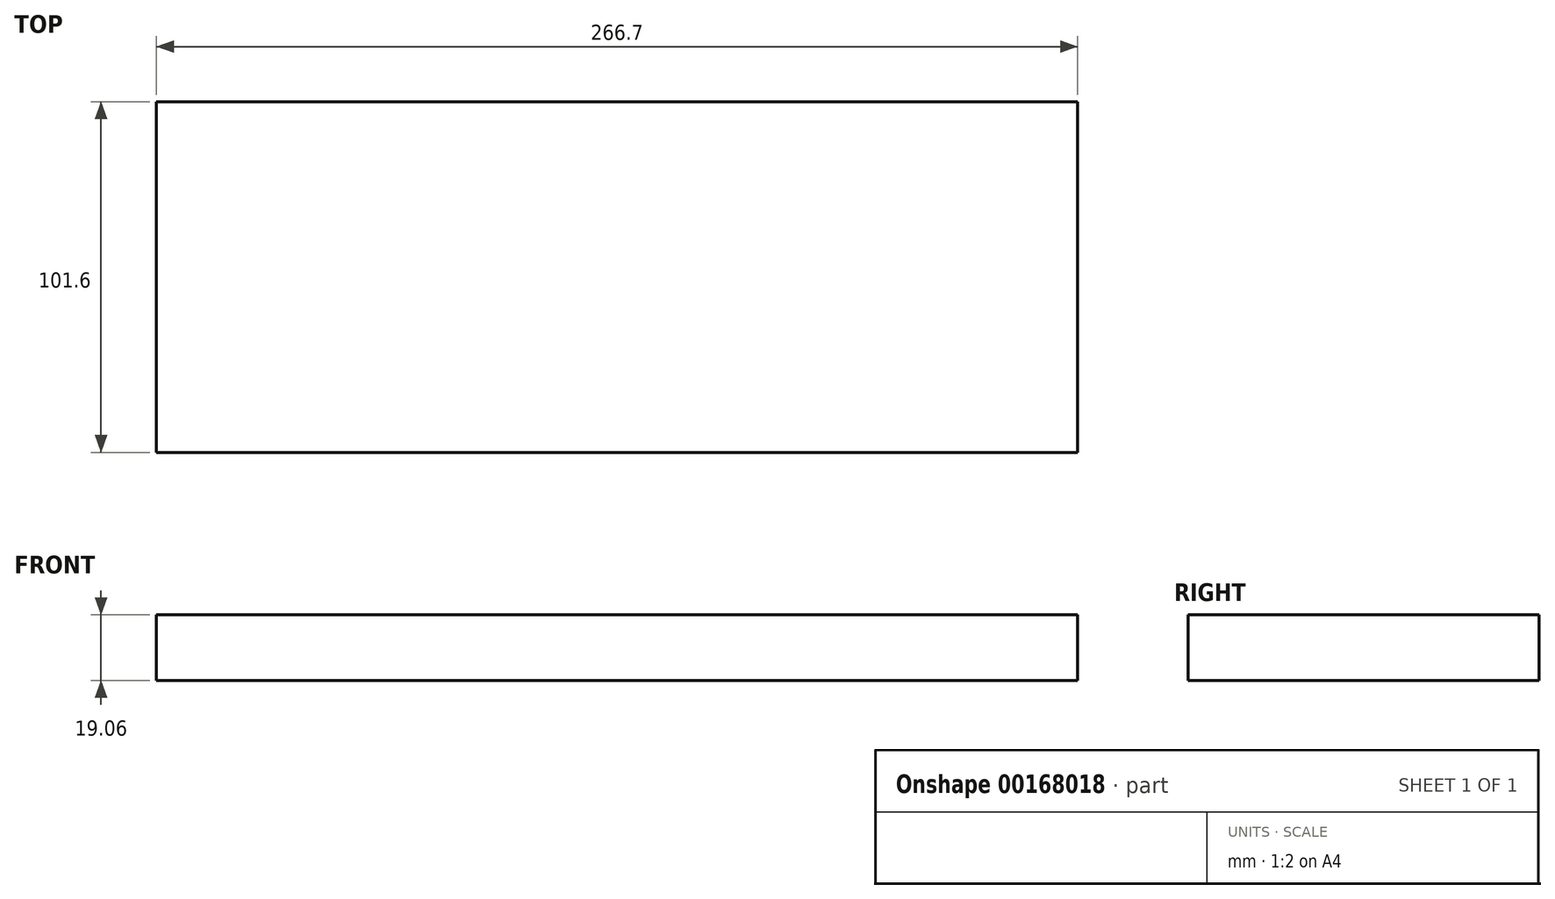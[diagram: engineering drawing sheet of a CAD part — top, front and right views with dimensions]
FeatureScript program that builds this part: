
annotation { "Feature Type Name" : "Feature", "Feature Type Description" : "" }
export const myFeature = defineFeature(function(context is Context, id is Id, definition is map)
    precondition{}
    {
        {
            var Q0;
            Q0=qCreatedBy(makeId("Right.planeOp"),FACE);
            var sketch = newSketch(context, id + "F0", { "sketchPlane" : qUnion([Q0])});
            skLineSegment(sketch, "E0.bottom", {"start": v(-50.8, 9.53) * mm, "end": v(50.8, 9.52) * mm});
            skLineSegment(sketch, "E0.top", {"start": v(-50.8, -9.52) * mm, "end": v(50.8, -9.53) * mm});
            skLineSegment(sketch, "E0.left", {"start": v(-50.8, 9.52) * mm, "end": v(-50.8, -9.52) * mm});
            skLineSegment(sketch, "E0.right", {"start": v(50.8, 9.53) * mm, "end": v(50.8, -9.53) * mm});
            skPoint(sketch, "E1", {"position": v(-50.8, 0) * mm});
            skPoint(sketch, "E2", {"position": v(0, 9.53) * mm});
            skSolve(sketch);
        }
        {
            var Q0;
            Q0 = qSketchRegion(id + "F0", true);
            extrude(context, id + "F1", {"entities" : qUnion([Q0]), "depth" : 266.7 * mm});
        }
    });
